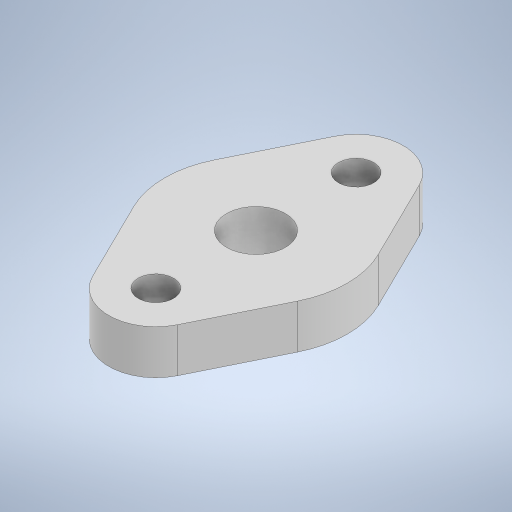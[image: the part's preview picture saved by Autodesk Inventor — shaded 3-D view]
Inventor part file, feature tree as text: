
AUTODESK INVENTOR PART (.ipt)
format: ipt  version: 2023.2 (Build 272271030, 271C)  size: 264,192 bytes
history: native  units: mm
features: extrude x1, sketch x1
ambient origin geometry x8: Origin, YZ Plane, XZ Plane, XY Plane, X Axis, Y Axis, Z Axis, Center Point
bodies: Solid1 (feature_tree)
feature tree (2):
  extrude  "Extrusion1"  Depth=15.0mm
  sketch  "Sketch1"  dims[d0=12.0mm d1=68.0mm d2=34.0mm d3=32.0mm d4=62.0mm d5=20.0mm d6=15.0mm d7=0.0mm]
